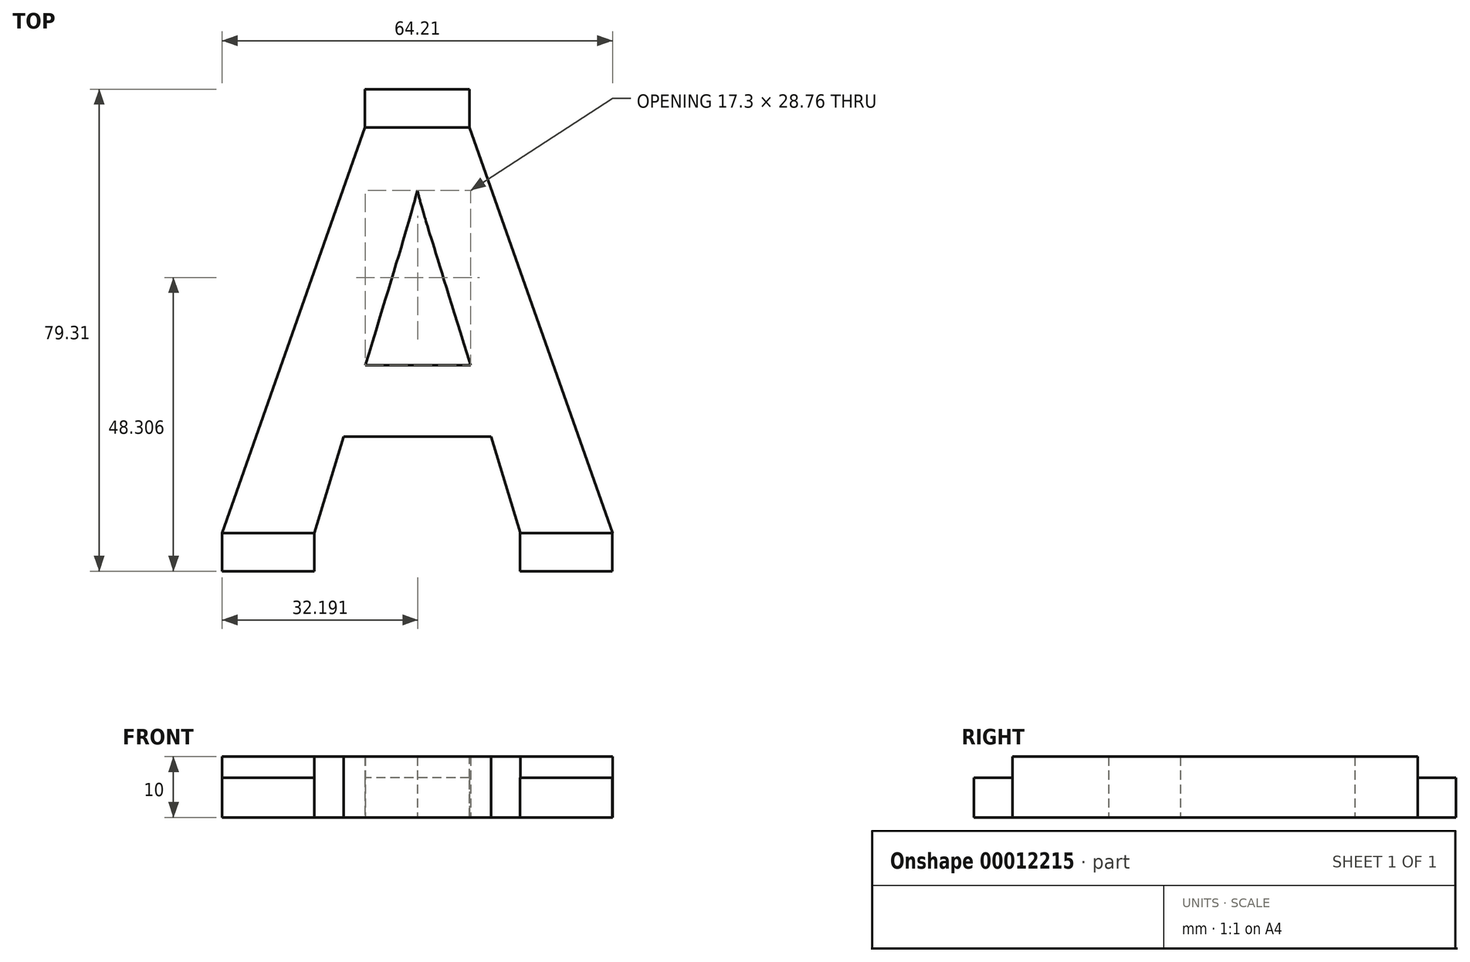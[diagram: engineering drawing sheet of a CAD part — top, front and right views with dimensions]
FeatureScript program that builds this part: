
annotation { "Feature Type Name" : "Feature", "Feature Type Description" : "" }
export const myFeature = defineFeature(function(context is Context, id is Id, definition is map)
    precondition{}
    {
        {
            var Q0;
            Q0=qCreatedBy(makeId("Top.planeOp"),FACE);
            var sketch = newSketch(context, id + "F0", { "sketchPlane" : qUnion([Q0])});
            skText(sketch, "E0", { "text": "A\n", "fontName": "OpenSans-Bold.ttf"});
            const initialGuessF0  = {"E0": [-0.0642, 0, 1, 0, 0.067]};
            skSetInitialGuess(sketch, initialGuessF0);
            skSolve(sketch);
        }
        {
            var Q0;
            Q0=makeQuery(id+"F0.imprint","IMPRINT",FACE,{"disambiguationData":[TD([[makeQuery(id+"F0.imprint","IMPRINT",EDGE,{"derivedFrom":sQuery(id+"F0.wireOp",EDGE,"E0.sketch_text.stroke-0")}),-1.0]])]});
            extrude(context, id + "F1", {"entities" : qUnion([Q0]), "depth" : 10 * mm});
        }
        {
            var Q0;
            Q0=makeQuery(id+"F1.opExtrude","SWEPT_FACE",FACE,{"disambiguationData":[OSD([sQuery(id+"F0.wireOp",EDGE,"E0.sketch_text.stroke-3")])]});
            var sketch = newSketch(context, id + "F2", { "sketchPlane" : qUnion([Q0])});
            skLineSegment(sketch, "E1.0.0", {"start": v(-64.2, 0) * mm, "end": v(-49.03, 0) * mm});
            skLineSegment(sketch, "E1.0.1", {"start": v(-49.03, 0) * mm, "end": v(-49.03, 10) * mm});
            skLineSegment(sketch, "E1.0.2", {"start": v(-49.03, 10) * mm, "end": v(-64.2, 10) * mm});
            skLineSegment(sketch, "E1.0.3", {"start": v(-64.2, 10) * mm, "end": v(-64.2, 0) * mm});
            skLineSegment(sketch, "E2.0.0", {"start": v(-15.18, 0) * mm, "end": v(0, 0) * mm});
            skLineSegment(sketch, "E2.0.1", {"start": v(0, 0) * mm, "end": v(0, 10) * mm});
            skLineSegment(sketch, "E2.0.2", {"start": v(0, 10) * mm, "end": v(-15.18, 10) * mm});
            skLineSegment(sketch, "E2.0.3", {"start": v(-15.18, 10) * mm, "end": v(-15.18, 0) * mm});
            skLineSegment(sketch, "E3.top", {"start": v(-64.2, 6.5) * mm, "end": v(-49.03, 6.5) * mm});
            skLineSegment(sketch, "E3.left", {"start": v(-64.2, 0) * mm, "end": v(-64.2, 6.5) * mm});
            skLineSegment(sketch, "E3.right", {"start": v(-49.03, 0) * mm, "end": v(-49.03, 6.5) * mm});
            skLineSegment(sketch, "E4.top", {"start": v(-15.18, 6.5) * mm, "end": v(0, 6.5) * mm});
            skLineSegment(sketch, "E4.left", {"start": v(-15.18, 0) * mm, "end": v(-15.18, 6.5) * mm});
            skLineSegment(sketch, "E4.right", {"start": v(0, 0) * mm, "end": v(0, 6.5) * mm});
            skSolve(sketch);
        }
        {
            var Q0;
            Q0=makeQuery(id+"F2.imprint","IMPRINT",FACE,{"disambiguationData":[TD([[makeQuery(id+"F2.imprint","IMPRINT",EDGE,{"derivedFrom":sQuery(id+"F2.wireOp",EDGE,"E1.0.0")}),-1.0]])]});
            var Q1;
            Q1=makeQuery(id+"F2.imprint","IMPRINT",FACE,{"disambiguationData":[TD([[makeQuery(id+"F2.imprint","IMPRINT",EDGE,{"derivedFrom":sQuery(id+"F2.wireOp",EDGE,"E2.0.0")}),1.0]])]});
            extrude(context, id + "F3", {"entities" : qUnion([Q0, Q1]), "operationType" : NewBodyOperationType.ADD, "depth" : 6.3 * mm});
        }
        {
            var Q0;
            Q0=makeQuery(id+"F1.opExtrude","SWEPT_FACE",FACE,{"disambiguationData":[OSD([sQuery(id+"F0.wireOp",EDGE,"E0.sketch_text.stroke-5")])]});
            var sketch = newSketch(context, id + "F4", { "sketchPlane" : qUnion([Q0])});
            skLineSegment(sketch, "E5.0.0", {"start": v(23.54, 0) * mm, "end": v(40.76, 0) * mm});
            skLineSegment(sketch, "E5.0.1", {"start": v(40.76, 0) * mm, "end": v(40.76, 10) * mm});
            skLineSegment(sketch, "E5.0.2", {"start": v(40.76, 10) * mm, "end": v(23.54, 10) * mm});
            skLineSegment(sketch, "E5.0.3", {"start": v(23.54, 10) * mm, "end": v(23.54, 0) * mm});
            skLineSegment(sketch, "E6.top", {"start": v(23.54, 6.5) * mm, "end": v(40.76, 6.5) * mm});
            skLineSegment(sketch, "E6.left", {"start": v(23.54, 0) * mm, "end": v(23.54, 6.5) * mm});
            skLineSegment(sketch, "E6.right", {"start": v(40.76, 0) * mm, "end": v(40.76, 6.5) * mm});
            skSolve(sketch);
        }
        {
            var Q0;
            Q0=makeQuery(id+"F4.imprint","IMPRINT",FACE,{"disambiguationData":[TD([[makeQuery(id+"F4.imprint","IMPRINT",EDGE,{"derivedFrom":sQuery(id+"F4.wireOp",EDGE,"E5.0.0")}),-1.0]])]});
            extrude(context, id + "F5", {"entities" : qUnion([Q0]), "operationType" : NewBodyOperationType.ADD, "depth" : 6.3 * mm});
        }
    });
